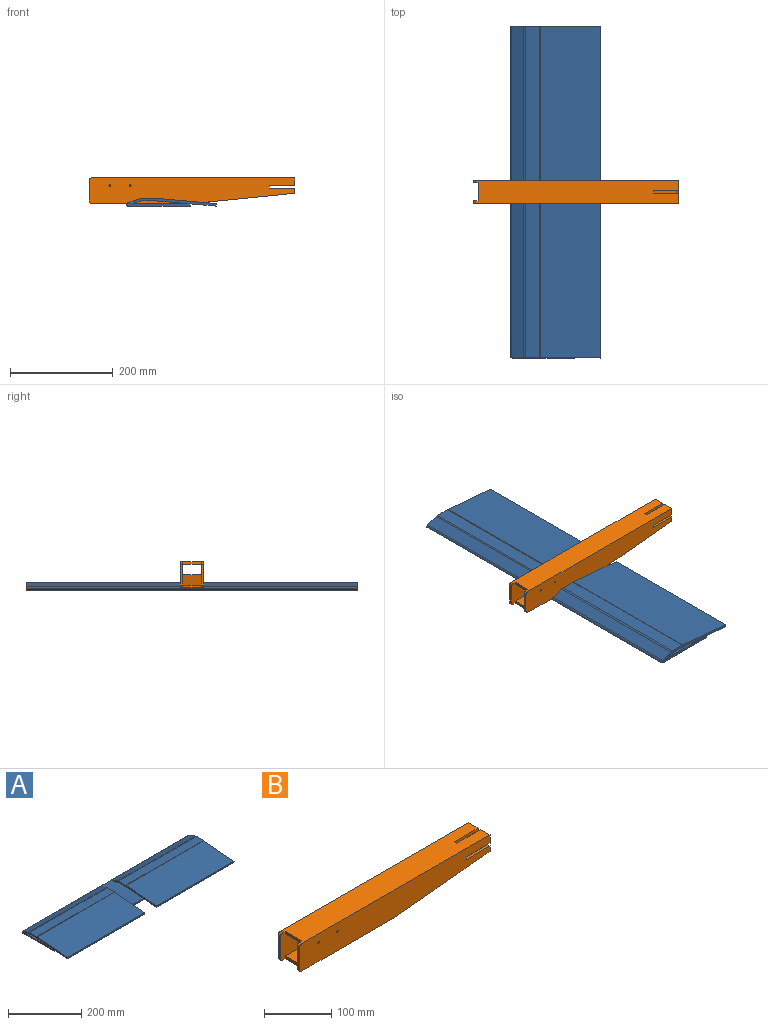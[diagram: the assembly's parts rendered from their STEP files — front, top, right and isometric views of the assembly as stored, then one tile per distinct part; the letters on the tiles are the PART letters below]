
ASSEMBLY  parts=2 mates=1
PART A: 33 faces, bbox 645x175.6x15.3 mm
  f0: plane 645x5mm, normal (0,-1,0), area 2874.3mm2, adj f1,f2,f5,f11,f12,f21,f27,f28
  f1: plane 645x123.57mm, normal (0,0,1), area 67781.1mm2, adj f0,f3,f4,f11,f12,f14,f19,f20
  f2: plane 645x120mm, normal (0,0,-1), area 77400mm2, adj f0,f11,f13,f27
  f3: plane 300x59.26mm, normal (0,0.09,-1), area 17845.6mm2, adj f1,f11,f12,f18
  f4: plane 300x12.8mm, normal (0,-0.34,-0.94), area 4085.3mm2, adj f1,f11,f12,f17
  f5: plane 300x50.47mm, normal (0,0.09,-1), area 15198.8mm2, adj f0,f6,f11,f12
  f6: plane 300x4.96mm, normal (0,-1,-0.09), area 1494.3mm2, adj f5,f7,f11,f12
  f7: plane 300x116.84mm, normal (0,-0.09,1), area 35186.9mm2, adj f6,f11,f12,f16
  f8: plane 300x27.36mm, normal (0,0,1), area 8209.1mm2, adj f11,f12,f15,f16
  f9: plane 300x23.24mm, normal (0,0.34,0.94), area 7420.7mm2, adj f11,f12,f14,f15
  f10: plane 300x26.48mm, normal (0,0,-1), area 7944.6mm2, adj f11,f12,f17,f18
  f11: plane 175.59x15.26mm, normal (-1,0,0), area 1464.5mm2, adj f0,f1,f2,f3,f4,f5,f6,f7
  f12: plane 174.47x15.26mm, normal (1,0,0), area 846.1mm2, adj f0,f1,f3,f4,f5,f6,f7,f8
  f13: cylinder r=5mm len=645mm, axis (-1,0,0), area 3912.3mm2, adj f2,f11,f14,f27
  f14: cylinder r=5mm len=645mm, axis (-1,0,0), area 2686.2mm2, adj f1,f9,f11,f12,f13,f25,f27,f28
  f15: cylinder r=10mm len=300mm, axis (1,0,0), area 1047.2mm2, adj f8,f9,f11,f12
  f16: cylinder r=20mm len=300mm, axis (1,0,0), area 523.6mm2, adj f7,f8,f11,f12
  f17: cylinder r=10mm len=300mm, axis (-1,0,0), area 1047.2mm2, adj f4,f10,f11,f12
  f18: cylinder r=20mm len=300mm, axis (1,0,0), area 523.6mm2, adj f3,f10,f11,f12
  f19: plane 300x59.26mm, normal (0,0.09,-1), area 17845.6mm2, adj f1,f27,f28,f32
  f20: plane 300x12.8mm, normal (0,-0.34,-0.94), area 4085.3mm2, adj f1,f27,f28,f31
  f21: plane 300x50.47mm, normal (0,0.09,-1), area 15198.8mm2, adj f0,f22,f27,f28
  f22: plane 300x4.96mm, normal (0,-1,-0.09), area 1494.3mm2, adj f21,f23,f27,f28
  f23: plane 300x116.84mm, normal (0,-0.09,1), area 35186.9mm2, adj f22,f27,f28,f30
  f24: plane 300x27.36mm, normal (0,0,1), area 8209.1mm2, adj f27,f28,f29,f30
  f25: plane 300x23.24mm, normal (0,0.34,0.94), area 7420.7mm2, adj f14,f27,f28,f29
  f26: plane 300x26.48mm, normal (0,0,-1), area 7944.6mm2, adj f27,f28,f31,f32
  f27: plane 175.59x15.26mm, normal (1,0,0), area 1464.5mm2, adj f0,f1,f2,f13,f14,f19,f20,f21
  f28: plane 174.47x15.26mm, normal (-1,0,0), area 846.1mm2, adj f0,f1,f14,f19,f20,f21,f22,f23
  f29: cylinder r=10mm len=300mm, axis (-1,0,0), area 1047.2mm2, adj f24,f25,f27,f28
  f30: cylinder r=20mm len=300mm, axis (-1,0,0), area 523.6mm2, adj f23,f24,f27,f28
  f31: cylinder r=10mm len=300mm, axis (1,0,0), area 1047.2mm2, adj f20,f26,f27,f28
  f32: cylinder r=20mm len=300mm, axis (-1,0,0), area 523.6mm2, adj f19,f26,f27,f28
PART B: 35 faces, bbox 400x45x50 mm
  f0: plane 40x5mm, normal (-1,0,0), area 200mm2, adj f10,f14,f27,f28
  f1: plane 395x45mm, normal (0,0,1), area 17350mm2, adj f2,f8,f9,f10,f13,f14,f22,f23
  f2: plane 20x15mm, normal (1,0,0), area 150mm2, adj f1,f3,f9,f13,f19,f22
  f3: plane 390x35mm, normal (0,0,-1), area 13400mm2, adj f2,f8,f13,f14,f22,f23,f24,f26
  f4: plane 45x10mm, normal (1,0,0), area 258.4mm2, adj f7,f9,f10,f13,f14,f15,f16,f21
  f5: plane 40x5mm, normal (-1,0,0), area 200mm2, adj f9,f13,f29,f30
  f6: plane 195x45mm, normal (0,0,-1), area 8600mm2, adj f7,f9,f10,f13,f14,f25,f28,f29
  f7: plane 200x45mm, normal (0.1,0,-1), area 9044.9mm2, adj f4,f6,f9,f10
  f8: plane 20x15mm, normal (1,0,0), area 150mm2, adj f1,f3,f10,f14,f18,f23
  f9: plane 400x50mm, normal (0,-1,0), area 17725.1mm2, adj f1,f2,f4,f5,f6,f7,f19,f20
  f10: plane 400x50mm, normal (0,1,0), area 17725.1mm2, adj f0,f1,f4,f6,f7,f8,f16,f17
  f11: plane 189.75x35mm, normal (0,0,1), area 6641.3mm2, adj f12,f13,f14,f25
  f12: plane 195.25x35mm, normal (-0.1,0,1), area 6867.8mm2, adj f11,f13,f14,f15
  f13: plane 400x50mm, normal (0,1,0), area 13821.4mm2, adj f1,f2,f3,f4,f5,f6,f11,f12
  f14: plane 400x50mm, normal (0,-1,0), area 13821.4mm2, adj f0,f1,f3,f4,f6,f8,f11,f12
  f15: plane 35x5mm, normal (0,0,1), area 175mm2, adj f4,f12,f13,f14
  f16: plane 50x5mm, normal (0,0,1), area 250mm2, adj f4,f10,f14,f17
  f17: plane 5x5mm, normal (1,0,0), area 25mm2, adj f10,f14,f16,f18
  f18: plane 50x5mm, normal (0,0,-1), area 250mm2, adj f8,f10,f14,f17
  f19: plane 50x5mm, normal (0,0,-1), area 250mm2, adj f2,f9,f13,f20
  f20: plane 5x5mm, normal (1,0,0), area 25mm2, adj f9,f13,f19,f21
  f21: plane 50x5mm, normal (0,0,1), area 250mm2, adj f4,f9,f13,f20
  f22: plane 50x5mm, normal (0,1,0), area 250mm2, adj f1,f2,f3,f24
  f23: plane 50x5mm, normal (0,-1,0), area 250mm2, adj f1,f3,f8,f24
  f24: plane 5x5mm, normal (1,0,0), area 25mm2, adj f1,f3,f22,f23
  f25: plane 35x5mm, normal (-1,0,0), area 175mm2, adj f6,f11,f13,f14
  f26: plane 35x5mm, normal (-1,0,0), area 175mm2, adj f1,f3,f13,f14
  f27: cylinder r=5mm len=5mm, axis (0,1,0), area 39.3mm2, adj f0,f1,f10,f14
  f28: cylinder r=5mm len=5mm, axis (0,-1,0), area 39.3mm2, adj f0,f6,f10,f14
  f29: cylinder r=5mm len=5mm, axis (0,-1,0), area 39.3mm2, adj f5,f6,f9,f13
  f30: cylinder r=5mm len=5mm, axis (0,1,0), area 39.3mm2, adj f1,f5,f9,f13
  f31: cylinder r=1.5mm len=5mm, axis (0,-1,0), area 47.1mm2, adj f10,f14
  f32: cylinder r=1.5mm len=5mm, axis (0,-1,0), area 47.1mm2, adj f10,f14
  f33: cylinder r=1.5mm len=5mm, axis (0,-1,0), area 47.1mm2, adj f9,f13
  f34: cylinder r=1.5mm len=5mm, axis (0,-1,0), area 47.1mm2, adj f9,f13
PLACE A rot(axis=(0,0,1),90deg) t=(245.74,34.39,-144.15)mm
PLACE B t=(48.96,56.89,-139.15)mm
MATE fastened B.f6 <-> A.f1  axis (0,0,-1) through (183.96,11.89,-139.15)mm
